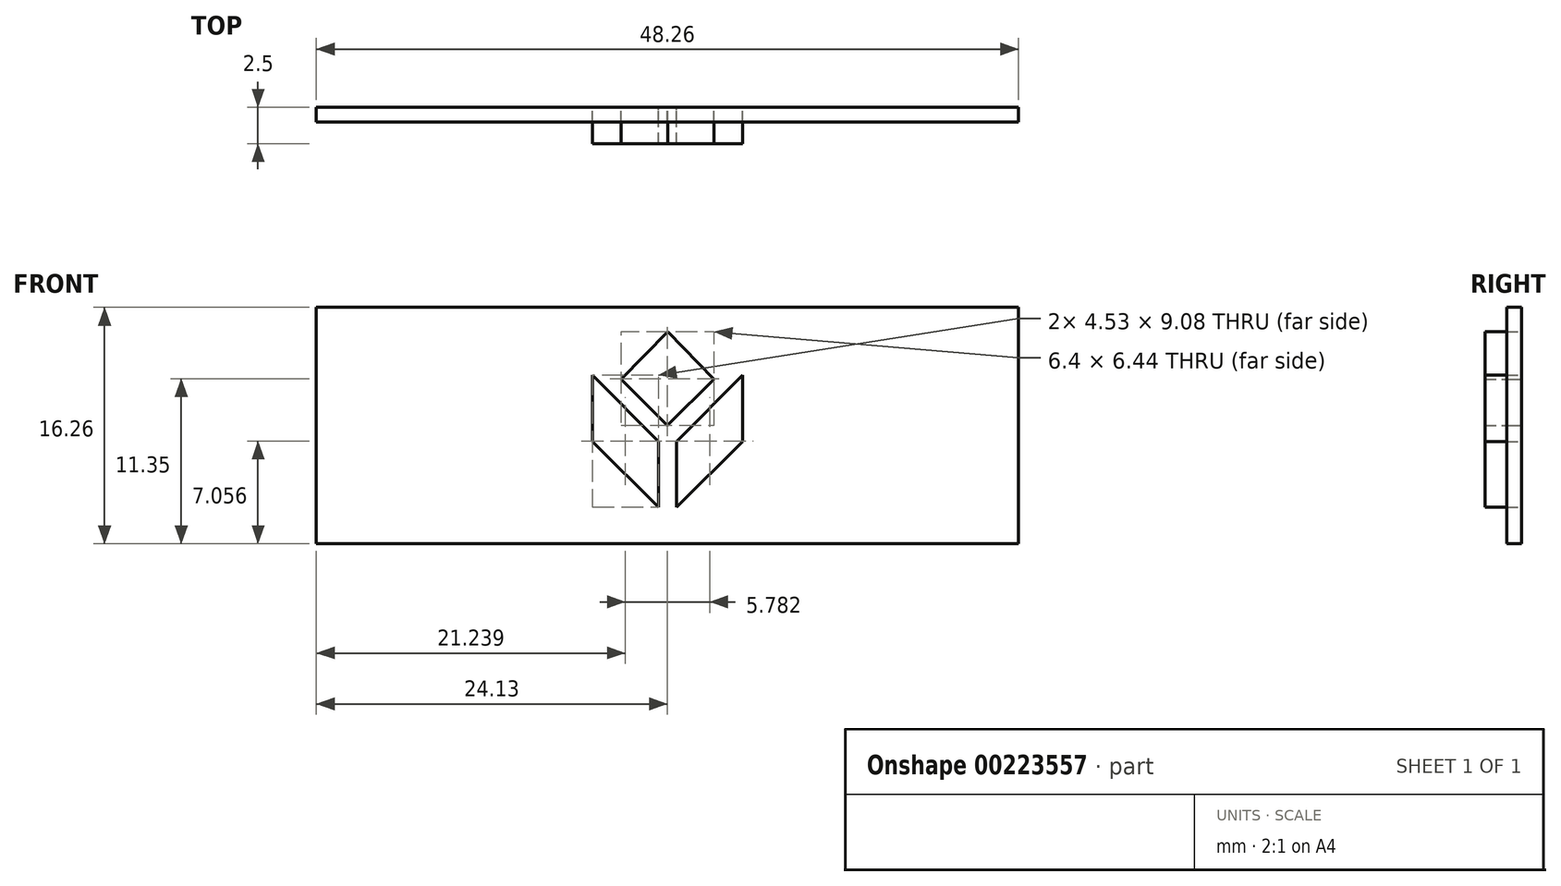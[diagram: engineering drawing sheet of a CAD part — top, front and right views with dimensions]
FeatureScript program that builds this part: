
annotation { "Feature Type Name" : "Feature", "Feature Type Description" : "" }
export const myFeature = defineFeature(function(context is Context, id is Id, definition is map)
    precondition{}
    {
        {
            var Q0;
            Q0=qCreatedBy(makeId("Front.planeOp"),FACE);
            var sketch = newSketch(context, id + "F0", { "sketchPlane" : qUnion([Q0])});
            skLineSegment(sketch, "E0.bottom", {"start": v(24.13, -8.13) * mm, "end": v(-24.13, -8.13) * mm});
            skLineSegment(sketch, "E0.top", {"start": v(24.13, 8.13) * mm, "end": v(-24.13, 8.13) * mm});
            skLineSegment(sketch, "E0.left", {"start": v(24.13, -8.13) * mm, "end": v(24.13, 8.13) * mm});
            skLineSegment(sketch, "E0.right", {"start": v(-24.13, -8.13) * mm, "end": v(-24.13, 8.13) * mm});
            skPoint(sketch, "E0.middle", {"position": v(0, 0) * mm});
            skLineSegment(sketch, "E1", {"start": v(-5.16, 3.47) * mm, "end": v(-5.16, -1.09) * mm, "construction": true});
            skLineSegment(sketch, "E2", {"start": v(-5.16, -1.09) * mm, "end": v(-0.63, -5.61) * mm, "construction": true});
            skLineSegment(sketch, "E3", {"start": v(-0.63, -5.61) * mm, "end": v(-0.63, -1.1) * mm, "construction": true});
            skLineSegment(sketch, "E4", {"start": v(-0.63, -1.1) * mm, "end": v(-5.16, 3.47) * mm, "construction": true});
            skLineSegment(sketch, "E5", {"start": v(0, 0) * mm, "end": v(-3.2, 3.18) * mm, "construction": true});
            skLineSegment(sketch, "E6", {"start": v(-3.2, 3.18) * mm, "end": v(0, 6.44) * mm, "construction": true});
            skPoint(sketch, "E6.endSnap0", {"position": v(-0.02, 6.44) * mm});
            skLineSegment(sketch, "E7.MirrorCS", {"start": v(3.2, 3.18) * mm, "end": v(0, 6.44) * mm, "construction": true});
            skLineSegment(sketch, "E8.MirrorCS", {"start": v(0, 0) * mm, "end": v(3.2, 3.18) * mm, "construction": true});
            skLineSegment(sketch, "E9.MirrorCS", {"start": v(0.63, -1.1) * mm, "end": v(5.16, 3.47) * mm, "construction": true});
            skLineSegment(sketch, "E10.MirrorCS", {"start": v(5.16, 3.47) * mm, "end": v(5.16, -1.09) * mm, "construction": true});
            skLineSegment(sketch, "E11.MirrorCS", {"start": v(5.16, -1.09) * mm, "end": v(0.63, -5.61) * mm, "construction": true});
            skLineSegment(sketch, "E12.MirrorCS", {"start": v(0.63, -5.61) * mm, "end": v(0.63, -1.1) * mm, "construction": true});
            skPoint(sketch, "E13.MirrorP", {"position": v(0.02, 6.44) * mm});
            skLineSegment(sketch, "E14", {"start": v(0.02, 6.44) * mm, "end": v(3.2, 3.18) * mm});
            skLineSegment(sketch, "E15", {"start": v(0, 0) * mm, "end": v(-3.2, 3.18) * mm});
            skLineSegment(sketch, "E16", {"start": v(0.02, 6.44) * mm, "end": v(-3.2, 3.18) * mm});
            skLineSegment(sketch, "E17", {"start": v(0, 0) * mm, "end": v(3.2, 3.18) * mm});
            skLineSegment(sketch, "E18", {"start": v(-5.16, 3.47) * mm, "end": v(-0.63, -1.1) * mm});
            skLineSegment(sketch, "E19", {"start": v(-0.63, -1.1) * mm, "end": v(-0.63, -5.61) * mm});
            skLineSegment(sketch, "E20", {"start": v(-0.63, -5.61) * mm, "end": v(-5.16, -1.09) * mm});
            skLineSegment(sketch, "E21", {"start": v(-5.16, -1.09) * mm, "end": v(-5.16, 3.47) * mm});
            skLineSegment(sketch, "E22", {"start": v(0.63, -1.1) * mm, "end": v(0.63, -5.61) * mm});
            skLineSegment(sketch, "E23", {"start": v(0.63, -5.61) * mm, "end": v(5.16, -1.09) * mm});
            skLineSegment(sketch, "E24", {"start": v(5.16, -1.09) * mm, "end": v(5.16, 3.47) * mm});
            skLineSegment(sketch, "E25", {"start": v(5.16, 3.47) * mm, "end": v(0.63, -1.1) * mm});
            skSolve(sketch);
        }
        {
            var Q0;
            Q0=makeQuery(id+"F0.imprint","IMPRINT",FACE,{"disambiguationData":[TD([[makeQuery(id+"F0.imprint","IMPRINT",EDGE,{"derivedFrom":sQuery(id+"F0.wireOp",EDGE,"E18")}),-1.0]])]});
            var Q1;
            Q1=makeQuery(id+"F0.imprint","IMPRINT",FACE,{"disambiguationData":[TD([[makeQuery(id+"F0.imprint","IMPRINT",EDGE,{"derivedFrom":sQuery(id+"F0.wireOp",EDGE,"E14")}),-1.0]])]});
            var Q2;
            Q2=makeQuery(id+"F0.imprint","IMPRINT",FACE,{"disambiguationData":[TD([[makeQuery(id+"F0.imprint","IMPRINT",EDGE,{"derivedFrom":sQuery(id+"F0.wireOp",EDGE,"E22")}),1.0]])]});
            extrude(context, id + "F1", {"entities" : qUnion([Q0, Q1, Q2]), "depth" : 2.5 * mm});
        }
        {
            var Q0;
            Q0=qSketchRegion(id+"F0",true);
            extrude(context, id + "F2", {"entities" : qUnion([Q0]), "depth" : 1 * mm});
        }
    });
